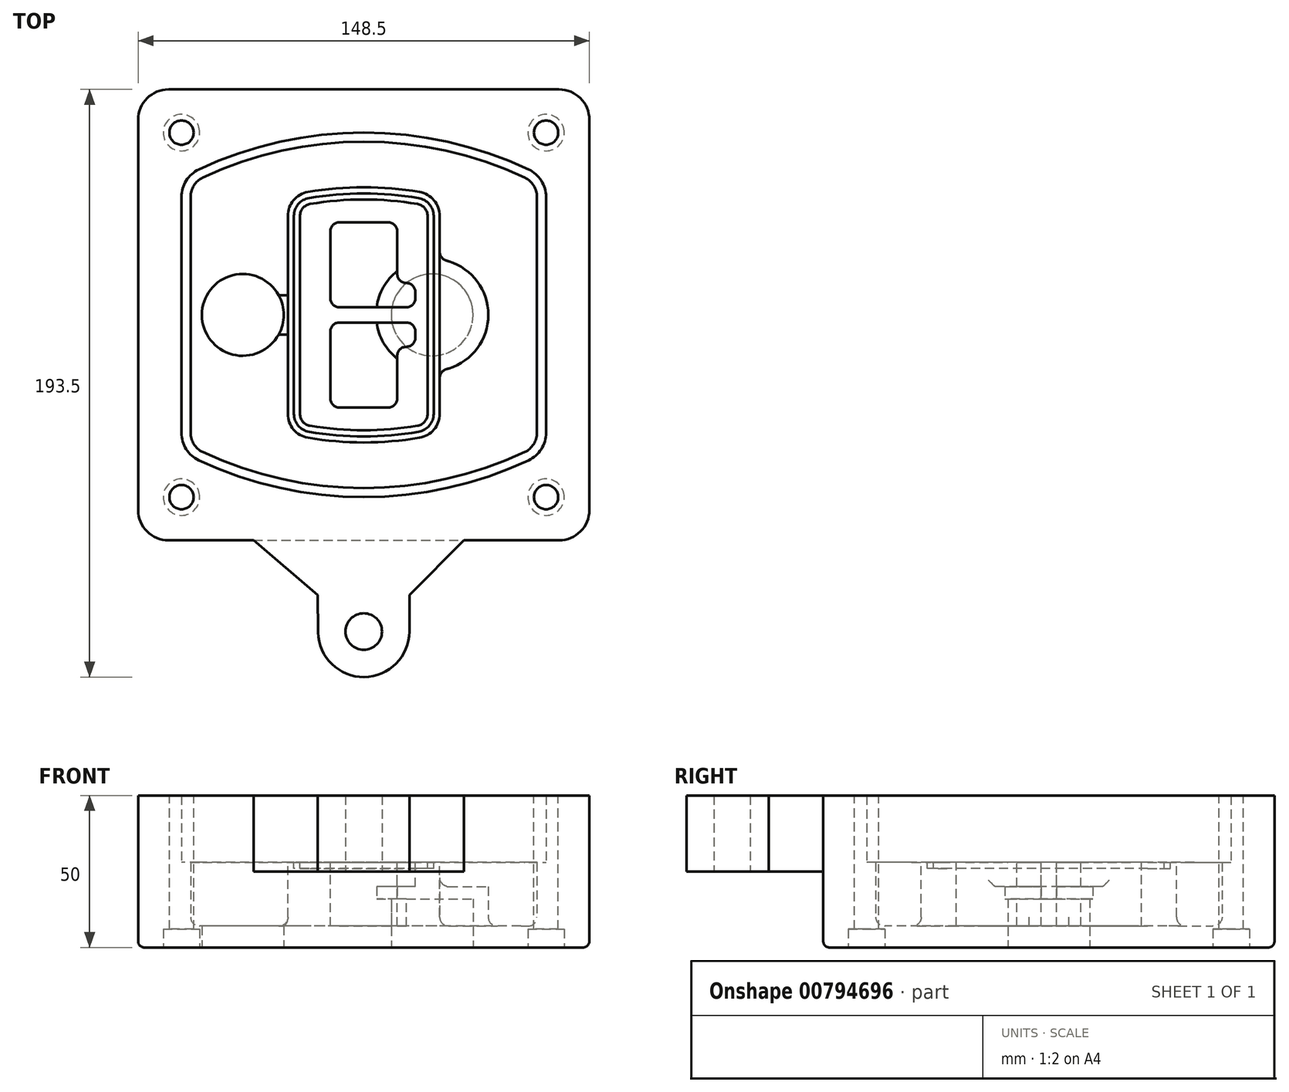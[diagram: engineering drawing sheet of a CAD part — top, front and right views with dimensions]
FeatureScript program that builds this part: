
annotation { "Feature Type Name" : "Feature", "Feature Type Description" : "" }
export const myFeature = defineFeature(function(context is Context, id is Id, definition is map)
    precondition{}
    {
        {
            var Q0;
            Q0=qCreatedBy(makeId("Top.planeOp"),FACE);
            var sketch = newSketch(context, id + "F0", { "sketchPlane" : qUnion([Q0])});
            skPoint(sketch, "E0.rect.middle", {"position": v(0, 0) * mm});
            skLineSegment(sketch, "E1.bottom", {"start": v(-64.25, -74.25) * mm, "end": v(64.25, -74.25) * mm});
            skLineSegment(sketch, "E1.top", {"start": v(-64.25, 74.25) * mm, "end": v(64.25, 74.25) * mm});
            skLineSegment(sketch, "E1.left", {"start": v(-74.25, -64.25) * mm, "end": v(-74.25, 64.25) * mm});
            skLineSegment(sketch, "E1.right", {"start": v(74.25, -64.25) * mm, "end": v(74.25, 64.25) * mm});
            skLineSegment(sketch, "E2", {"start": v(-74.25, 74.25) * mm, "end": v(74.25, -74.25) * mm, "construction": true});
            skLineSegment(sketch, "E3", {"start": v(74.25, 74.25) * mm, "end": v(-74.25, -74.25) * mm, "construction": true});
            skCircle(sketch, "E4", {"center": v(-60, 60) * mm, "radius": 4 * mm});
            skCircle(sketch, "E5", {"center": v(60, 60) * mm, "radius": 4 * mm});
            skCircle(sketch, "E6", {"center": v(60, -60) * mm, "radius": 4 * mm});
            skCircle(sketch, "E7", {"center": v(-60, -60) * mm, "radius": 4 * mm});
            skLineSegment(sketch, "E8", {"start": v(-60, 60) * mm, "end": v(60, 60) * mm, "construction": true});
            skLineSegment(sketch, "E9", {"start": v(60, 60) * mm, "end": v(60, -60) * mm, "construction": true});
            skLineSegment(sketch, "E10", {"start": v(60, -60) * mm, "end": v(-60, -60) * mm, "construction": true});
            skLineSegment(sketch, "E11", {"start": v(-60, -60) * mm, "end": v(-60, 60) * mm, "construction": true});
            skLineSegment(sketch, "E12", {"start": v(-60, 38.83) * mm, "end": v(-60, -38.83) * mm});
            skLineSegment(sketch, "E13", {"start": v(60, 38.83) * mm, "end": v(60, -38.83) * mm});
            skArc(sketch, "E14", {"start": v(54.26, 47.88) * mm, "mid": v(0, 60) * mm, "end": v(-54.26, 47.88) * mm});
            skArc(sketch, "E15", {"start": v(-54.26, -47.88) * mm, "mid": v(0, -60) * mm, "end": v(54.26, -47.88) * mm});
            skLineSegment(sketch, "E16", {"start": v(-60, 0) * mm, "end": v(60, 0) * mm, "construction": true});
            skPoint(sketch, "E17.visualSharp", {"position": v(-60, -45) * mm});
            skArc(sketch, "E17.filletArc", {"start": v(-60, -38.83) * mm, "mid": v(-58.44, -44.2) * mm, "end": v(-54.26, -47.88) * mm});
            skPoint(sketch, "E18.visualSharp", {"position": v(-60, 45) * mm});
            skArc(sketch, "E18.filletArc", {"start": v(-54.26, 47.88) * mm, "mid": v(-58.44, 44.2) * mm, "end": v(-60, 38.83) * mm});
            skPoint(sketch, "E19.visualSharp", {"position": v(60, 45) * mm});
            skArc(sketch, "E19.filletArc", {"start": v(60, 38.83) * mm, "mid": v(58.44, 44.2) * mm, "end": v(54.26, 47.88) * mm});
            skPoint(sketch, "E20.visualSharp", {"position": v(60, -45) * mm});
            skArc(sketch, "E20.filletArc", {"start": v(54.26, -47.88) * mm, "mid": v(58.44, -44.2) * mm, "end": v(60, -38.83) * mm});
            skPoint(sketch, "E21.visualSharp", {"position": v(-74.25, 74.25) * mm});
            skArc(sketch, "E21.filletArc", {"start": v(-64.25, 74.25) * mm, "mid": v(-71.32, 71.32) * mm, "end": v(-74.25, 64.25) * mm});
            skPoint(sketch, "E22.visualSharp", {"position": v(74.25, 74.25) * mm});
            skArc(sketch, "E22.filletArc", {"start": v(74.25, 64.25) * mm, "mid": v(71.32, 71.32) * mm, "end": v(64.25, 74.25) * mm});
            skPoint(sketch, "E23.visualSharp", {"position": v(74.25, -74.25) * mm});
            skArc(sketch, "E23.filletArc", {"start": v(64.25, -74.25) * mm, "mid": v(71.32, -71.32) * mm, "end": v(74.25, -64.25) * mm});
            skPoint(sketch, "E24.visualSharp", {"position": v(-74.25, -74.25) * mm});
            skArc(sketch, "E24.filletArc", {"start": v(-74.25, -64.25) * mm, "mid": v(-71.32, -71.32) * mm, "end": v(-64.25, -74.25) * mm});
            skArc(sketch, "E25.0", {"start": v(57, 38.83) * mm, "mid": v(55.9, 42.58) * mm, "end": v(52.98, 45.17) * mm});
            skLineSegment(sketch, "E25.1", {"start": v(57, 38.83) * mm, "end": v(57, -38.83) * mm});
            skArc(sketch, "E25.2", {"start": v(52.98, -45.17) * mm, "mid": v(55.9, -42.58) * mm, "end": v(57, -38.83) * mm});
            skArc(sketch, "E25.3", {"start": v(-52.98, -45.17) * mm, "mid": v(0, -57) * mm, "end": v(52.98, -45.17) * mm});
            skArc(sketch, "E25.4", {"start": v(-57, -38.83) * mm, "mid": v(-55.9, -42.58) * mm, "end": v(-52.98, -45.17) * mm});
            skArc(sketch, "E25.5", {"start": v(52.98, 45.17) * mm, "mid": v(0, 57) * mm, "end": v(-52.98, 45.17) * mm});
            skLineSegment(sketch, "E25.6", {"start": v(-57, 38.83) * mm, "end": v(-57, -38.83) * mm});
            skArc(sketch, "E25.7", {"start": v(-52.98, 45.17) * mm, "mid": v(-55.9, 42.58) * mm, "end": v(-57, 38.83) * mm});
            skArc(sketch, "E26.0", {"start": v(-55.96, 51.5) * mm, "mid": v(-61.82, 46.33) * mm, "end": v(-64, 38.83) * mm});
            skArc(sketch, "E26.1", {"start": v(55.96, 51.5) * mm, "mid": v(0, 64) * mm, "end": v(-55.96, 51.5) * mm});
            skArc(sketch, "E26.2", {"start": v(64, 38.83) * mm, "mid": v(61.82, 46.33) * mm, "end": v(55.96, 51.5) * mm});
            skLineSegment(sketch, "E26.3", {"start": v(64, 38.83) * mm, "end": v(64, -38.83) * mm});
            skArc(sketch, "E26.4", {"start": v(55.96, -51.5) * mm, "mid": v(61.82, -46.33) * mm, "end": v(64, -38.83) * mm});
            skLineSegment(sketch, "E26.5", {"start": v(-64, 38.83) * mm, "end": v(-64, -38.83) * mm});
            skArc(sketch, "E26.6", {"start": v(-55.96, -51.5) * mm, "mid": v(0, -64) * mm, "end": v(55.96, -51.5) * mm});
            skArc(sketch, "E26.7", {"start": v(-64, -38.83) * mm, "mid": v(-61.82, -46.33) * mm, "end": v(-55.96, -51.5) * mm});
            skSolve(sketch);
        }
        {
            var Q0;
            Q0=makeQuery(id+"F0.imprint","IMPRINT",FACE,{"disambiguationData":[TD([[makeQuery(id+"F0.imprint","IMPRINT",EDGE,{"derivedFrom":sQuery(id+"F0.wireOp",EDGE,"E1.bottom")}),1.0]])]});
            var Q1;
            Q1=makeQuery(id+"F0.imprint","IMPRINT",FACE,{"disambiguationData":[TD([[makeQuery(id+"F0.imprint","IMPRINT",EDGE,{"derivedFrom":sQuery(id+"F0.wireOp",EDGE,"E12")}),1.0]])]});
            var Q2;
            Q2=makeQuery(id+"F0.imprint","IMPRINT",FACE,{"disambiguationData":[TD([[makeQuery(id+"F0.imprint","IMPRINT",EDGE,{"derivedFrom":sQuery(id+"F0.wireOp",EDGE,"E25.0")}),1.0]])]});
            var Q3;
            Q3=makeQuery(id+"F0.imprint","IMPRINT",FACE,{"disambiguationData":[TD([[makeQuery(id+"F0.imprint","IMPRINT",EDGE,{"derivedFrom":sQuery(id+"F0.wireOp",EDGE,"E12")}),-1.0]])]});
            extrude(context, id + "F1", {"entities" : qUnion([Q0, Q1, Q2, Q3]), "oppositeDirection" : true, "depth" : 25 * mm, "offsetDistance" : 25 * mm});
        }
        {
            var Q0;
            Q0=makeQuery(id+"F0.imprint","IMPRINT",FACE,{"disambiguationData":[TD([[makeQuery(id+"F0.imprint","IMPRINT",EDGE,{"derivedFrom":sQuery(id+"F0.wireOp",EDGE,"E12")}),1.0]])]});
            extrude(context, id + "F2", {"entities" : qUnion([Q0]), "operationType" : NewBodyOperationType.ADD, "depth" : 3 * mm});
        }
        {
            var Q0;
            Q0=makeQuery(id+"F0.imprint","IMPRINT",FACE,{"disambiguationData":[TD([[makeQuery(id+"F0.imprint","IMPRINT",EDGE,{"derivedFrom":sQuery(id+"F0.wireOp",EDGE,"E25.0")}),1.0]])]});
            extrude(context, id + "F3", {"entities" : qUnion([Q0]), "operationType" : NewBodyOperationType.REMOVE, "oppositeDirection" : true, "depth" : 18 * mm});
        }
        {
            var Q0;
            Q0=makeQuery(id+"F2.opExtrude","CAP_FACE",FACE,{"disambiguationData":[OSD([sQuery(id+"F0.wireOp",EDGE,"E12"),sQuery(id+"F0.wireOp",EDGE,"E13"),sQuery(id+"F0.wireOp",EDGE,"E14"),sQuery(id+"F0.wireOp",EDGE,"E15"),sQuery(id+"F0.wireOp",EDGE,"E17.filletArc"),sQuery(id+"F0.wireOp",EDGE,"E18.filletArc"),sQuery(id+"F0.wireOp",EDGE,"E19.filletArc"),sQuery(id+"F0.wireOp",EDGE,"E20.filletArc"),sQuery(id+"F0.wireOp",EDGE,"E25.0"),sQuery(id+"F0.wireOp",EDGE,"E25.1"),sQuery(id+"F0.wireOp",EDGE,"E25.2"),sQuery(id+"F0.wireOp",EDGE,"E25.3"),sQuery(id+"F0.wireOp",EDGE,"E25.4"),sQuery(id+"F0.wireOp",EDGE,"E25.5"),sQuery(id+"F0.wireOp",EDGE,"E25.6"),sQuery(id+"F0.wireOp",EDGE,"E25.7")])],"isStart":false});
            var sketch = newSketch(context, id + "F4", { "sketchPlane" : qUnion([Q0])});
            skArc(sketch, "E27.0", {"start": v(-18.34, -40.45) * mm, "mid": v(0, -42) * mm, "end": v(18.34, -40.45) * mm});
            skArc(sketch, "E28.0", {"start": v(18.34, 40.45) * mm, "mid": v(0, 42) * mm, "end": v(-18.34, 40.45) * mm});
            skLineSegment(sketch, "E29", {"start": v(-25, 32.57) * mm, "end": v(-25, -32.57) * mm});
            skLineSegment(sketch, "E30", {"start": v(25, 32.57) * mm, "end": v(25, -32.57) * mm});
            skLineSegment(sketch, "E31", {"start": v(-25, 39.1) * mm, "end": v(25, 39.1) * mm, "construction": true});
            skLineSegment(sketch, "E32", {"start": v(-25, -39.1) * mm, "end": v(25, -39.1) * mm, "construction": true});
            skPoint(sketch, "E33.visualSharp", {"position": v(-25, 39.1) * mm});
            skArc(sketch, "E33.filletArc", {"start": v(-18.34, 40.45) * mm, "mid": v(-23.11, 37.73) * mm, "end": v(-25, 32.57) * mm});
            skPoint(sketch, "E34.visualSharp", {"position": v(25, 39.1) * mm});
            skArc(sketch, "E34.filletArc", {"start": v(25, 32.57) * mm, "mid": v(23.11, 37.73) * mm, "end": v(18.34, 40.45) * mm});
            skPoint(sketch, "E35.visualSharp", {"position": v(25, -39.1) * mm});
            skArc(sketch, "E35.filletArc", {"start": v(18.34, -40.45) * mm, "mid": v(23.11, -37.73) * mm, "end": v(25, -32.57) * mm});
            skPoint(sketch, "E36.visualSharp", {"position": v(-25, -39.1) * mm});
            skArc(sketch, "E36.filletArc", {"start": v(-25, -32.57) * mm, "mid": v(-23.11, -37.73) * mm, "end": v(-18.34, -40.45) * mm});
            skArc(sketch, "E37.0", {"start": v(52.98, 45.17) * mm, "mid": v(0, 57) * mm, "end": v(-52.98, 45.17) * mm});
            skArc(sketch, "E37.1", {"start": v(-52.98, 45.17) * mm, "mid": v(-55.9, 42.58) * mm, "end": v(-57, 38.83) * mm});
            skLineSegment(sketch, "E37.2", {"start": v(-57, 38.83) * mm, "end": v(-57, -38.83) * mm});
            skArc(sketch, "E37.3", {"start": v(-57, -38.83) * mm, "mid": v(-55.9, -42.58) * mm, "end": v(-52.98, -45.17) * mm});
            skArc(sketch, "E37.4", {"start": v(-52.98, -45.17) * mm, "mid": v(0, -57) * mm, "end": v(52.98, -45.17) * mm});
            skArc(sketch, "E37.5", {"start": v(52.98, -45.17) * mm, "mid": v(55.9, -42.58) * mm, "end": v(57, -38.83) * mm});
            skLineSegment(sketch, "E37.6", {"start": v(57, 38.83) * mm, "end": v(57, -38.83) * mm});
            skArc(sketch, "E37.7", {"start": v(57, 38.83) * mm, "mid": v(55.9, 42.58) * mm, "end": v(52.98, 45.17) * mm});
            skLineSegment(sketch, "E38.0", {"start": v(23, 32.57) * mm, "end": v(23, -32.57) * mm});
            skArc(sketch, "E38.1", {"start": v(18, -38.48) * mm, "mid": v(21.58, -36.44) * mm, "end": v(23, -32.57) * mm});
            skArc(sketch, "E38.2", {"start": v(-18, -38.48) * mm, "mid": v(0, -40) * mm, "end": v(18, -38.48) * mm});
            skArc(sketch, "E38.3", {"start": v(-23, -32.57) * mm, "mid": v(-21.58, -36.44) * mm, "end": v(-18, -38.48) * mm});
            skLineSegment(sketch, "E38.4", {"start": v(-23, 32.57) * mm, "end": v(-23, -32.57) * mm});
            skArc(sketch, "E38.5", {"start": v(23, 32.57) * mm, "mid": v(21.58, 36.44) * mm, "end": v(18, 38.48) * mm});
            skArc(sketch, "E38.6", {"start": v(-18, 38.48) * mm, "mid": v(-21.58, 36.44) * mm, "end": v(-23, 32.57) * mm});
            skArc(sketch, "E38.7", {"start": v(18, 38.48) * mm, "mid": v(0, 40) * mm, "end": v(-18, 38.48) * mm});
            skArc(sketch, "E39.0", {"start": v(21, 32.57) * mm, "mid": v(20.06, 35.15) * mm, "end": v(17.67, 36.5) * mm});
            skLineSegment(sketch, "E39.1", {"start": v(21, 32.57) * mm, "end": v(21, -32.57) * mm});
            skArc(sketch, "E39.2", {"start": v(17.67, -36.5) * mm, "mid": v(20.06, -35.15) * mm, "end": v(21, -32.57) * mm});
            skArc(sketch, "E39.3", {"start": v(-17.67, -36.5) * mm, "mid": v(0, -38) * mm, "end": v(17.67, -36.5) * mm});
            skArc(sketch, "E39.4", {"start": v(-21, -32.57) * mm, "mid": v(-20.06, -35.15) * mm, "end": v(-17.67, -36.5) * mm});
            skArc(sketch, "E39.5", {"start": v(17.67, 36.5) * mm, "mid": v(0, 38) * mm, "end": v(-17.67, 36.5) * mm});
            skLineSegment(sketch, "E39.6", {"start": v(-21, 32.57) * mm, "end": v(-21, -32.57) * mm});
            skArc(sketch, "E39.7", {"start": v(-17.67, 36.5) * mm, "mid": v(-20.06, 35.15) * mm, "end": v(-21, 32.57) * mm});
            skLineSegment(sketch, "E40", {"start": v(-25, 0) * mm, "end": v(25, 0) * mm, "construction": true});
            skLineSegment(sketch, "E41", {"start": v(-11, 5.5) * mm, "end": v(-11, 27.5) * mm});
            skLineSegment(sketch, "E42", {"start": v(-8, 30.5) * mm, "end": v(8, 30.5) * mm});
            skLineSegment(sketch, "E43", {"start": v(11, 27.5) * mm, "end": v(11, 13.5) * mm});
            skLineSegment(sketch, "E44", {"start": v(14, 10.5) * mm, "end": v(14, 10.5) * mm});
            skLineSegment(sketch, "E45", {"start": v(17, 7.5) * mm, "end": v(17, 5.5) * mm});
            skLineSegment(sketch, "E46", {"start": v(14, 2.5) * mm, "end": v(-8, 2.5) * mm});
            skPoint(sketch, "E47.visualSharp", {"position": v(-11, 30.5) * mm});
            skArc(sketch, "E47.filletArc", {"start": v(-8, 30.5) * mm, "mid": v(-10.12, 29.62) * mm, "end": v(-11, 27.5) * mm});
            skPoint(sketch, "E48.visualSharp", {"position": v(11, 30.5) * mm});
            skArc(sketch, "E48.filletArc", {"start": v(11, 27.5) * mm, "mid": v(10.12, 29.62) * mm, "end": v(8, 30.5) * mm});
            skPoint(sketch, "E49.visualSharp", {"position": v(11, 10.5) * mm});
            skArc(sketch, "E49.filletArc", {"start": v(11, 13.5) * mm, "mid": v(11.88, 11.38) * mm, "end": v(14, 10.5) * mm});
            skPoint(sketch, "E50.visualSharp", {"position": v(17, 10.5) * mm});
            skArc(sketch, "E50.filletArc", {"start": v(17, 7.5) * mm, "mid": v(16.12, 9.62) * mm, "end": v(14, 10.5) * mm});
            skPoint(sketch, "E51.visualSharp", {"position": v(17, 2.5) * mm});
            skArc(sketch, "E51.filletArc", {"start": v(14, 2.5) * mm, "mid": v(16.12, 3.38) * mm, "end": v(17, 5.5) * mm});
            skPoint(sketch, "E52.visualSharp", {"position": v(-11, 2.5) * mm});
            skArc(sketch, "E52.filletArc", {"start": v(-11, 5.5) * mm, "mid": v(-10.12, 3.38) * mm, "end": v(-8, 2.5) * mm});
            skLineSegment(sketch, "E53.0.MirrorCS", {"start": v(14, -2.5) * mm, "end": v(-8, -2.5) * mm});
            skArc(sketch, "E54.0.MirrorCS", {"start": v(-11, -5.5) * mm, "mid": v(-10.12, -3.38) * mm, "end": v(-8, -2.5) * mm});
            skLineSegment(sketch, "E55.0.MirrorCS", {"start": v(-11, -5.5) * mm, "end": v(-11, -27.5) * mm});
            skArc(sketch, "E56.0.MirrorCS", {"start": v(-8, -30.5) * mm, "mid": v(-10.12, -29.62) * mm, "end": v(-11, -27.5) * mm});
            skLineSegment(sketch, "E57.0.MirrorCS", {"start": v(-8, -30.5) * mm, "end": v(8, -30.5) * mm});
            skArc(sketch, "E58.0.MirrorCS", {"start": v(11, -27.5) * mm, "mid": v(10.12, -29.62) * mm, "end": v(8, -30.5) * mm});
            skLineSegment(sketch, "E59.0.MirrorCS", {"start": v(11, -27.5) * mm, "end": v(11, -13.5) * mm});
            skArc(sketch, "E60.0.MirrorCS", {"start": v(11, -13.5) * mm, "mid": v(11.88, -11.38) * mm, "end": v(14, -10.5) * mm});
            skArc(sketch, "E61.0.MirrorCS", {"start": v(17, -7.5) * mm, "mid": v(16.12, -9.62) * mm, "end": v(14, -10.5) * mm});
            skLineSegment(sketch, "E62.0.MirrorCS", {"start": v(17, -7.5) * mm, "end": v(17, -5.5) * mm});
            skArc(sketch, "E63.0.MirrorCS", {"start": v(14, -2.5) * mm, "mid": v(16.12, -3.38) * mm, "end": v(17, -5.5) * mm});
            skSolve(sketch);
        }
        {
            var Q0;
            Q0=makeQuery(id+"F4.imprint","IMPRINT",FACE,{"disambiguationData":[TD([[makeQuery(id+"F4.imprint","IMPRINT",EDGE,{"derivedFrom":sQuery(id+"F4.wireOp",EDGE,"E27.0")}),1.0]])]});
            var Q1;
            Q1=makeQuery(id+"F4.imprint","IMPRINT",FACE,{"disambiguationData":[TD([[makeQuery(id+"F4.imprint","IMPRINT",EDGE,{"derivedFrom":sQuery(id+"F4.wireOp",EDGE,"E38.0")}),-1.0]])]});
            var Q2;
            Q2=makeQuery(id+"F4.imprint","IMPRINT",FACE,{"disambiguationData":[TD([[makeQuery(id+"F4.imprint","IMPRINT",EDGE,{"derivedFrom":sQuery(id+"F4.wireOp",EDGE,"E39.0")}),1.0]])]});
            extrude(context, id + "F5", {"entities" : qUnion([Q0, Q1, Q2]), "operationType" : NewBodyOperationType.ADD, "endBound" : BoundingType.UP_TO_NEXT, "oppositeDirection" : true, "depth" : 25 * mm});
        }
        {
            var Q0;
            Q0=makeQuery(id+"F4.imprint","IMPRINT",FACE,{"disambiguationData":[TD([[makeQuery(id+"F4.imprint","IMPRINT",EDGE,{"derivedFrom":sQuery(id+"F4.wireOp",EDGE,"E38.0")}),-1.0]])]});
            extrude(context, id + "F6", {"entities" : qUnion([Q0]), "operationType" : NewBodyOperationType.REMOVE, "oppositeDirection" : true, "depth" : 2 * mm});
        }
        {
            var Q0;
            Q0=makeQuery(id+"F1.opExtrude","CAP_FACE",FACE,{"disambiguationData":[OSD([sQuery(id+"F0.wireOp",EDGE,"E1.bottom"),sQuery(id+"F0.wireOp",EDGE,"E1.top"),sQuery(id+"F0.wireOp",EDGE,"E1.left"),sQuery(id+"F0.wireOp",EDGE,"E1.right"),sQuery(id+"F0.wireOp",EDGE,"E4"),sQuery(id+"F0.wireOp",EDGE,"E5"),sQuery(id+"F0.wireOp",EDGE,"E6"),sQuery(id+"F0.wireOp",EDGE,"E7"),sQuery(id+"F0.wireOp",EDGE,"E21.filletArc"),sQuery(id+"F0.wireOp",EDGE,"E22.filletArc"),sQuery(id+"F0.wireOp",EDGE,"E23.filletArc"),sQuery(id+"F0.wireOp",EDGE,"E24.filletArc")])],"isStart":false});
            var sketch = newSketch(context, id + "F7", { "sketchPlane" : qUnion([Q0])});
            skCircle(sketch, "E64", {"center": v(22.5, 0) * mm, "radius": 13.47 * mm});
            skCircle(sketch, "E65", {"center": v(-39.81, 0) * mm, "radius": 13.47 * mm});
            skLineSegment(sketch, "E66", {"start": v(74.25, 0) * mm, "end": v(-74.25, 0) * mm});
            skCircle(sketch, "E67", {"center": v(22.5, 0) * mm, "radius": 18.47 * mm});
            skCircle(sketch, "E68", {"center": v(60, -60) * mm, "radius": 6 * mm});
            skCircle(sketch, "E69", {"center": v(-60, -60) * mm, "radius": 6 * mm});
            skCircle(sketch, "E70", {"center": v(-60, 60) * mm, "radius": 6 * mm});
            skCircle(sketch, "E71", {"center": v(60, 60) * mm, "radius": 6 * mm});
            skSolve(sketch);
        }
        {
            var Q0;
            {var subQ1=sQuery(id+"F7.wireOp",EDGE,"E66");var subQ4=sQuery(id+"F7.wireOp",EDGE,"E64");var subQ6=makeQuery(id+"F7.imprint","INTERSECT",VERTEX,{"disambiguationData":[OD(0.0)],"derivedFrom":[subQ4,subQ1]});Q0=makeQuery(id+"F7.imprint","IMPRINT",FACE,{"disambiguationData":[TD([[makeQuery(id+"F7.imprint","IMPRINT",EDGE,{"disambiguationData":[TD([[subQ6,-1.0]])],"derivedFrom":subQ4}),-1.0]])]});}
            var Q1;
            {var subQ0=sQuery(id+"F7.wireOp",EDGE,"E66");var subQ1=sQuery(id+"F7.wireOp",EDGE,"E64");var subQ3=makeQuery(id+"F7.imprint","INTERSECT",VERTEX,{"disambiguationData":[OD(0.0)],"derivedFrom":[subQ1,subQ0]});Q1=makeQuery(id+"F7.imprint","IMPRINT",FACE,{"disambiguationData":[TD([[makeQuery(id+"F7.imprint","IMPRINT",EDGE,{"disambiguationData":[TD([[subQ3,-1.0]])],"derivedFrom":subQ1}),1.0]])]});}
            var Q2;
            {var subQ0=sQuery(id+"F7.wireOp",EDGE,"E66");var subQ1=sQuery(id+"F7.wireOp",EDGE,"E64");var subQ3=makeQuery(id+"F7.imprint","INTERSECT",VERTEX,{"disambiguationData":[OD(0.0)],"derivedFrom":[subQ1,subQ0]});Q2=makeQuery(id+"F7.imprint","IMPRINT",FACE,{"disambiguationData":[TD([[makeQuery(id+"F7.imprint","IMPRINT",EDGE,{"disambiguationData":[TD([[subQ3,1.0]])],"derivedFrom":subQ1}),1.0]])]});}
            var Q3;
            {var subQ1=sQuery(id+"F7.wireOp",EDGE,"E66");var subQ4=sQuery(id+"F7.wireOp",EDGE,"E64");var subQ6=makeQuery(id+"F7.imprint","INTERSECT",VERTEX,{"disambiguationData":[OD(0.0)],"derivedFrom":[subQ4,subQ1]});Q3=makeQuery(id+"F7.imprint","IMPRINT",FACE,{"disambiguationData":[TD([[makeQuery(id+"F7.imprint","IMPRINT",EDGE,{"disambiguationData":[TD([[subQ6,1.0]])],"derivedFrom":subQ4}),-1.0]])]});}
            extrude(context, id + "F8", {"entities" : qUnion([Q0, Q1, Q2, Q3]), "operationType" : NewBodyOperationType.ADD, "oppositeDirection" : true, "depth" : 20 * mm});
        }
        {
            var Q0;
            {var subQ0=sQuery(id+"F7.wireOp",EDGE,"E66");var subQ1=sQuery(id+"F7.wireOp",EDGE,"E64");var subQ3=makeQuery(id+"F7.imprint","INTERSECT",VERTEX,{"disambiguationData":[OD(0.0)],"derivedFrom":[subQ1,subQ0]});Q0=makeQuery(id+"F7.imprint","IMPRINT",FACE,{"disambiguationData":[TD([[makeQuery(id+"F7.imprint","IMPRINT",EDGE,{"disambiguationData":[TD([[subQ3,-1.0]])],"derivedFrom":subQ1}),1.0]])]});}
            var Q1;
            {var subQ0=sQuery(id+"F7.wireOp",EDGE,"E66");var subQ1=sQuery(id+"F7.wireOp",EDGE,"E64");var subQ3=makeQuery(id+"F7.imprint","INTERSECT",VERTEX,{"disambiguationData":[OD(0.0)],"derivedFrom":[subQ1,subQ0]});Q1=makeQuery(id+"F7.imprint","IMPRINT",FACE,{"disambiguationData":[TD([[makeQuery(id+"F7.imprint","IMPRINT",EDGE,{"disambiguationData":[TD([[subQ3,1.0]])],"derivedFrom":subQ1}),1.0]])]});}
            extrude(context, id + "F9", {"entities" : qUnion([Q0, Q1]), "operationType" : NewBodyOperationType.REMOVE, "oppositeDirection" : true, "depth" : 16 * mm});
        }
        {
            var Q0;
            {var subQ0=sQuery(id+"F7.wireOp",EDGE,"E66");var subQ1=sQuery(id+"F7.wireOp",EDGE,"E65");var subQ3=makeQuery(id+"F7.imprint","INTERSECT",VERTEX,{"disambiguationData":[OD(0.0)],"derivedFrom":[subQ1,subQ0]});Q0=makeQuery(id+"F7.imprint","IMPRINT",FACE,{"disambiguationData":[TD([[makeQuery(id+"F7.imprint","IMPRINT",EDGE,{"disambiguationData":[TD([[subQ3,-1.0]])],"derivedFrom":subQ1}),1.0]])]});}
            var Q1;
            {var subQ0=sQuery(id+"F7.wireOp",EDGE,"E66");var subQ1=sQuery(id+"F7.wireOp",EDGE,"E65");var subQ3=makeQuery(id+"F7.imprint","INTERSECT",VERTEX,{"disambiguationData":[OD(0.0)],"derivedFrom":[subQ1,subQ0]});Q1=makeQuery(id+"F7.imprint","IMPRINT",FACE,{"disambiguationData":[TD([[makeQuery(id+"F7.imprint","IMPRINT",EDGE,{"disambiguationData":[TD([[subQ3,1.0]])],"derivedFrom":subQ1}),1.0]])]});}
            extrude(context, id + "F10", {"entities" : qUnion([Q0, Q1]), "operationType" : NewBodyOperationType.REMOVE, "oppositeDirection" : true, "depth" : 25 * mm});
        }
        {
            var Q0;
            Q0=makeQuery(id+"F7.imprint","IMPRINT",FACE,{"disambiguationData":[TD([[makeQuery(id+"F7.imprint","IMPRINT",EDGE,{"derivedFrom":sQuery(id+"F7.wireOp",EDGE,"E68")}),1.0]])]});
            var Q1;
            Q1=makeQuery(id+"F7.imprint","IMPRINT",FACE,{"disambiguationData":[TD([[makeQuery(id+"F7.imprint","IMPRINT",EDGE,{"derivedFrom":makeQuery(id+"F1.opExtrude","CAP_EDGE",EDGE,{"disambiguationData":[OSD([sQuery(id+"F0.wireOp",EDGE,"E5")])],"isStart":false})}),-1.0]])]});
            var Q2;
            Q2=makeQuery(id+"F7.imprint","IMPRINT",FACE,{"disambiguationData":[TD([[makeQuery(id+"F7.imprint","IMPRINT",EDGE,{"derivedFrom":sQuery(id+"F7.wireOp",EDGE,"E69")}),1.0]])]});
            var Q3;
            Q3=makeQuery(id+"F7.imprint","IMPRINT",FACE,{"disambiguationData":[TD([[makeQuery(id+"F7.imprint","IMPRINT",EDGE,{"derivedFrom":makeQuery(id+"F1.opExtrude","CAP_EDGE",EDGE,{"disambiguationData":[OSD([sQuery(id+"F0.wireOp",EDGE,"E4")])],"isStart":false})}),-1.0]])]});
            var Q4;
            Q4=makeQuery(id+"F7.imprint","IMPRINT",FACE,{"disambiguationData":[TD([[makeQuery(id+"F7.imprint","IMPRINT",EDGE,{"derivedFrom":sQuery(id+"F7.wireOp",EDGE,"E70")}),1.0]])]});
            var Q5;
            Q5=makeQuery(id+"F7.imprint","IMPRINT",FACE,{"disambiguationData":[TD([[makeQuery(id+"F7.imprint","IMPRINT",EDGE,{"derivedFrom":makeQuery(id+"F1.opExtrude","CAP_EDGE",EDGE,{"disambiguationData":[OSD([sQuery(id+"F0.wireOp",EDGE,"E7")])],"isStart":false})}),-1.0]])]});
            var Q6;
            Q6=makeQuery(id+"F7.imprint","IMPRINT",FACE,{"disambiguationData":[TD([[makeQuery(id+"F7.imprint","IMPRINT",EDGE,{"derivedFrom":sQuery(id+"F7.wireOp",EDGE,"E71")}),1.0]])]});
            var Q7;
            Q7=makeQuery(id+"F7.imprint","IMPRINT",FACE,{"disambiguationData":[TD([[makeQuery(id+"F7.imprint","IMPRINT",EDGE,{"derivedFrom":makeQuery(id+"F1.opExtrude","CAP_EDGE",EDGE,{"disambiguationData":[OSD([sQuery(id+"F0.wireOp",EDGE,"E6")])],"isStart":false})}),-1.0]])]});
            extrude(context, id + "F11", {"entities" : qUnion([Q0, Q1, Q2, Q3, Q4, Q5, Q6, Q7]), "operationType" : NewBodyOperationType.REMOVE, "oppositeDirection" : true, "depth" : 6 * mm});
        }
        {
            var Q0;
            Q0=makeQuery(id+"F9.boolean.opBoolean","COPY",FACE,{"derivedFrom":makeQuery(id+"F9.opExtrude","CAP_FACE",FACE,{"disambiguationData":[OSD([sQuery(id+"F7.wireOp",EDGE,"E64")])],"isStart":false})});
            var sketch = newSketch(context, id + "F12", { "sketchPlane" : qUnion([Q0])});
            skArc(sketch, "E72.0", {"start": v(11, 14.45) * mm, "mid": v(6.45, 9.13) * mm, "end": v(4.2, 2.5) * mm});
            skArc(sketch, "E72.1", {"start": v(4.2, -2.5) * mm, "mid": v(6.45, -9.13) * mm, "end": v(11, -14.45) * mm});
            skLineSegment(sketch, "E73", {"start": v(4.2, -2.5) * mm, "end": v(14, -2.5) * mm});
            skLineSegment(sketch, "E74.0", {"start": v(14, 2.5) * mm, "end": v(4.2, 2.5) * mm});
            skArc(sketch, "E74.1", {"start": v(14, 2.5) * mm, "mid": v(16.12, 3.38) * mm, "end": v(17, 5.5) * mm});
            skLineSegment(sketch, "E74.2", {"start": v(17, 7.5) * mm, "end": v(17, 5.5) * mm});
            skArc(sketch, "E74.3", {"start": v(17, 7.5) * mm, "mid": v(16.12, 9.62) * mm, "end": v(14, 10.5) * mm});
            skArc(sketch, "E74.4", {"start": v(11, 13.5) * mm, "mid": v(11.88, 11.38) * mm, "end": v(14, 10.5) * mm});
            skLineSegment(sketch, "E74.5", {"start": v(11, 14.45) * mm, "end": v(11, 13.5) * mm});
            skLineSegment(sketch, "E74.7", {"start": v(14, -2.5) * mm, "end": v(4.2, -2.5) * mm});
            skArc(sketch, "E74.8", {"start": v(14, -2.5) * mm, "mid": v(16.12, -3.38) * mm, "end": v(17, -5.5) * mm});
            skLineSegment(sketch, "E74.9", {"start": v(17, -7.5) * mm, "end": v(17, -5.5) * mm});
            skArc(sketch, "E74.10", {"start": v(17, -7.5) * mm, "mid": v(16.12, -9.62) * mm, "end": v(14, -10.5) * mm});
            skArc(sketch, "E74.11", {"start": v(11, -13.5) * mm, "mid": v(11.88, -11.38) * mm, "end": v(14, -10.5) * mm});
            skLineSegment(sketch, "E74.12", {"start": v(11, -14.45) * mm, "end": v(11, -13.5) * mm});
            skPoint(sketch, "E75.orphan", {"position": v(11, -27.5) * mm});
            skPoint(sketch, "E76.orphan", {"position": v(-8, -2.5) * mm});
            skPoint(sketch, "E77.orphan", {"position": v(-8, 2.5) * mm});
            skPoint(sketch, "E78.orphan", {"position": v(11, 27.5) * mm});
            skSolve(sketch);
        }
        {
            var Q0;
            {var subQ7=sQuery(id+"F12.wireOp",EDGE,"E72.0");var subQ14=sQuery(id+"F12.wireOp",EDGE,"E72.1");var subQ16=sQuery(id+"F12.wireOp",EDGE,"E74.1");var subQ18=sQuery(id+"F12.wireOp",EDGE,"E74.8");Q0=qUnion([makeQuery(id+"F12.imprint","IMPRINT",FACE,{"disambiguationData":[TD([[makeQuery(id+"F12.imprint","IMPRINT",EDGE,{"derivedFrom":subQ7}),1.0]])]}),makeQuery(id+"F12.imprint","IMPRINT",FACE,{"disambiguationData":[TD([[makeQuery(id+"F12.imprint","IMPRINT",EDGE,{"derivedFrom":subQ14}),1.0]])]}),makeQuery(id+"F12.imprint","IMPRINT",FACE,{"disambiguationData":[TD([[makeQuery(id+"F12.imprint","IMPRINT",EDGE,{"derivedFrom":subQ16}),1.0]])]}),makeQuery(id+"F12.imprint","IMPRINT",FACE,{"disambiguationData":[TD([[makeQuery(id+"F12.imprint","IMPRINT",EDGE,{"derivedFrom":subQ18}),-1.0]])]})]);}
            var Q1;
            Q1=makeQuery(id+"F5.boolean.opBoolean","SPLIT",FACE,{"disambiguationData":[TD([makeQuery(id+"F5.opExtrude","SWEPT_FACE",FACE,{"disambiguationData":[OSD([sQuery(id+"F4.wireOp",EDGE,"E41")])]})])],"derivedFrom":makeQuery(id+"F3.boolean.opBoolean","COPY",FACE,{"derivedFrom":makeQuery(id+"F3.opExtrude","CAP_FACE",FACE,{"disambiguationData":[OSD([sQuery(id+"F0.wireOp",EDGE,"E25.0"),sQuery(id+"F0.wireOp",EDGE,"E25.1"),sQuery(id+"F0.wireOp",EDGE,"E25.2"),sQuery(id+"F0.wireOp",EDGE,"E25.3"),sQuery(id+"F0.wireOp",EDGE,"E25.4"),sQuery(id+"F0.wireOp",EDGE,"E25.5"),sQuery(id+"F0.wireOp",EDGE,"E25.6"),sQuery(id+"F0.wireOp",EDGE,"E25.7")])],"isStart":false})})});
            extrude(context, id + "F13", {"entities" : qUnion([Q0]), "operationType" : NewBodyOperationType.REMOVE, "endBound" : BoundingType.UP_TO_SURFACE, "endBoundEntityFace" : qUnion([Q1]), "depth" : 25 * mm});
        }
        {
            var Q0;
            Q0=makeQuery(id+"F3.boolean.opBoolean","COPY",EDGE,{"derivedFrom":makeQuery(id+"F3.opExtrude","CAP_EDGE",EDGE,{"disambiguationData":[OSD([sQuery(id+"F0.wireOp",EDGE,"E25.6")])],"isStart":false})});
            var Q1;
            Q1=makeQuery(id+"F8.boolean.opBoolean","INTERSECT",EDGE,{"derivedFrom":[makeQuery(id+"F5.opExtrude","SWEPT_FACE",FACE,{"disambiguationData":[OSD([sQuery(id+"F4.wireOp",EDGE,"E30")])]}),makeQuery(id+"F8.opExtrude","CAP_FACE",FACE,{"disambiguationData":[OSD([sQuery(id+"F7.wireOp",EDGE,"E67")])],"isStart":false})]});
            var Q2;
            Q2=makeQuery(id+"F8.boolean.opBoolean","INTERSECT",EDGE,{"disambiguationData":[OD(1.0)],"derivedFrom":[makeQuery(id+"F5.opExtrude","SWEPT_FACE",FACE,{"disambiguationData":[OSD([sQuery(id+"F4.wireOp",EDGE,"E30")])]}),makeQuery(id+"F8.opExtrude","SWEPT_FACE",FACE,{"disambiguationData":[OSD([sQuery(id+"F7.wireOp",EDGE,"E67")])]})]});
            var Q3;
            {var subQ0=sQuery(id+"F4.wireOp",EDGE,"E30");Q3=makeQuery(id+"F8.boolean.opBoolean","SPLIT",EDGE,{"disambiguationData":[TD([makeQuery(id+"F5.opExtrude","SWEPT_FACE",FACE,{"disambiguationData":[OSD([sQuery(id+"F4.wireOp",EDGE,"E35.filletArc")])]})])],"derivedFrom":makeQuery(id+"F5.opExtrude","CAP_EDGE",EDGE,{"disambiguationData":[OSD([subQ0])],"isStart":false})});}
            var Q4;
            {var subQ0=sQuery(id+"F0.wireOp",EDGE,"E25.7");var subQ1=sQuery(id+"F0.wireOp",EDGE,"E25.1");var subQ2=sQuery(id+"F0.wireOp",EDGE,"E25.6");var subQ3=sQuery(id+"F0.wireOp",EDGE,"E25.5");var subQ4=sQuery(id+"F0.wireOp",EDGE,"E25.4");var subQ5=sQuery(id+"F0.wireOp",EDGE,"E25.0");var subQ6=sQuery(id+"F0.wireOp",EDGE,"E25.2");var subQ7=sQuery(id+"F0.wireOp",EDGE,"E25.3");Q4=makeQuery(id+"F8.boolean.opBoolean","INTERSECT",EDGE,{"derivedFrom":[makeQuery(id+"F5.boolean.opBoolean","SPLIT",FACE,{"disambiguationData":[TD([makeQuery(id+"F2.opExtrude","SWEPT_FACE",FACE,{"disambiguationData":[OSD([subQ5])]})])],"derivedFrom":makeQuery(id+"F3.boolean.opBoolean","COPY",FACE,{"derivedFrom":makeQuery(id+"F3.opExtrude","CAP_FACE",FACE,{"disambiguationData":[OSD([subQ5,subQ1,subQ6,subQ7,subQ4,subQ3,subQ2,subQ0])],"isStart":false})})}),makeQuery(id+"F8.opExtrude","SWEPT_FACE",FACE,{"disambiguationData":[OSD([sQuery(id+"F7.wireOp",EDGE,"E67")])]})]});}
            var Q5;
            Q5=makeQuery(id+"F8.boolean.opBoolean","INTERSECT",EDGE,{"disambiguationData":[OD(0.0)],"derivedFrom":[makeQuery(id+"F5.opExtrude","SWEPT_FACE",FACE,{"disambiguationData":[OSD([sQuery(id+"F4.wireOp",EDGE,"E30")])]}),makeQuery(id+"F8.opExtrude","SWEPT_FACE",FACE,{"disambiguationData":[OSD([sQuery(id+"F7.wireOp",EDGE,"E67")])]})]});
            fillet(context, id + "F14", {"entities" : qUnion([Q0, Q1, Q2, Q3, Q4, Q5]), "radius" : 3 * mm, "tangentPropagation" : true, "allowEdgeOverflow" : false});
        }
        {
            var Q0;
            Q0=makeQuery(id+"F1.opExtrude","CAP_EDGE",EDGE,{"disambiguationData":[OSD([sQuery(id+"F0.wireOp",EDGE,"E1.bottom")])],"isStart":false});
            fillet(context, id + "F15", {"entities" : qUnion([Q0]), "radius" : 2 * mm, "tangentPropagation" : true, "allowEdgeOverflow" : false});
        }
        {
            var Q0;
            {var subQ0=sQuery(id+"F0.wireOp",EDGE,"E21.filletArc");var subQ1=sQuery(id+"F0.wireOp",EDGE,"E7");var subQ2=sQuery(id+"F0.wireOp",EDGE,"E6");var subQ3=sQuery(id+"F0.wireOp",EDGE,"E5");var subQ4=sQuery(id+"F0.wireOp",EDGE,"E4");var subQ5=sQuery(id+"F0.wireOp",EDGE,"E22.filletArc");var subQ6=sQuery(id+"F0.wireOp",EDGE,"E1.bottom");var subQ7=sQuery(id+"F0.wireOp",EDGE,"E1.right");var subQ8=sQuery(id+"F0.wireOp",EDGE,"E1.top");var subQ9=sQuery(id+"F0.wireOp",EDGE,"E1.left");var subQ10=sQuery(id+"F0.wireOp",EDGE,"E23.filletArc");var subQ11=sQuery(id+"F0.wireOp",EDGE,"E24.filletArc");Q0=makeQuery(id+"F2.boolean.opBoolean","SPLIT",FACE,{"disambiguationData":[TD([makeQuery(id+"F1.opExtrude","SWEPT_FACE",FACE,{"disambiguationData":[OSD([subQ6])]})])],"derivedFrom":makeQuery(id+"F1.opExtrude","CAP_FACE",FACE,{"disambiguationData":[OSD([subQ6,subQ8,subQ9,subQ7,subQ4,subQ3,subQ2,subQ1,subQ0,subQ5,subQ10,subQ11])],"isStart":true})});}
            var sketch = newSketch(context, id + "F16", { "sketchPlane" : qUnion([Q0])});
            skCircle(sketch, "E79", {"center": v(0, -104.25) * mm, "radius": 6 * mm});
            skArc(sketch, "E80", {"start": v(-15, -104.52) * mm, "mid": v(0.14, -119.25) * mm, "end": v(15, -104.25) * mm});
            skLineSegment(sketch, "E81", {"start": v(-15, -104.52) * mm, "end": v(-15.22, -92.25) * mm});
            skLineSegment(sketch, "E82", {"start": v(15, -104.25) * mm, "end": v(15, -92.25) * mm});
            skLineSegment(sketch, "E83", {"start": v(-15.22, -92.25) * mm, "end": v(-36.28, -74.25) * mm});
            skLineSegment(sketch, "E84", {"start": v(15, -92.25) * mm, "end": v(33, -74.25) * mm});
            skLineSegment(sketch, "E85.0", {"start": v(-74.25, -64.25) * mm, "end": v(-74.25, 64.25) * mm});
            skArc(sketch, "E85.1", {"start": v(-64.25, 74.25) * mm, "mid": v(-71.32, 71.32) * mm, "end": v(-74.25, 64.25) * mm});
            skLineSegment(sketch, "E85.2", {"start": v(-64.25, 74.25) * mm, "end": v(64.25, 74.25) * mm});
            skLineSegment(sketch, "E85.3", {"start": v(74.25, -64.25) * mm, "end": v(74.25, 64.25) * mm});
            skArc(sketch, "E85.4", {"start": v(74.25, 64.25) * mm, "mid": v(71.32, 71.32) * mm, "end": v(64.25, 74.25) * mm});
            skArc(sketch, "E85.5", {"start": v(64.25, -74.25) * mm, "mid": v(71.32, -71.32) * mm, "end": v(74.25, -64.25) * mm});
            skLineSegment(sketch, "E85.6", {"start": v(-64.25, -74.25) * mm, "end": v(64.25, -74.25) * mm});
            skArc(sketch, "E85.7", {"start": v(-74.25, -64.25) * mm, "mid": v(-71.32, -71.32) * mm, "end": v(-64.25, -74.25) * mm});
            skCircle(sketch, "E85.8", {"center": v(-60, -60) * mm, "radius": 4 * mm});
            skCircle(sketch, "E85.9", {"center": v(60, -60) * mm, "radius": 4 * mm});
            skCircle(sketch, "E85.10", {"center": v(-60, 60) * mm, "radius": 4 * mm});
            skCircle(sketch, "E85.11", {"center": v(60, 60) * mm, "radius": 4 * mm});
            skPoint(sketch, "E85.12", {"position": v(71.32, 71.32) * mm});
            skLineSegment(sketch, "E86", {"start": v(-74.25, 0) * mm, "end": v(74.25, 0) * mm, "construction": true});
            skArc(sketch, "E87.MirrorCS", {"start": v(-15, 104.52) * mm, "mid": v(0.14, 119.25) * mm, "end": v(15, 104.25) * mm});
            skLineSegment(sketch, "E88.MirrorCS", {"start": v(-15, 104.52) * mm, "end": v(-15.22, 92.25) * mm});
            skArc(sketch, "E89.MirrorCS", {"start": v(64.25, 74.25) * mm, "mid": v(71.32, 71.32) * mm, "end": v(74.25, 64.25) * mm});
            skLineSegment(sketch, "E90.MirrorCS", {"start": v(-15.22, 92.25) * mm, "end": v(-36.28, 74.25) * mm});
            skLineSegment(sketch, "E91.MirrorCS", {"start": v(15, 104.25) * mm, "end": v(15, 92.25) * mm});
            skLineSegment(sketch, "E92.MirrorCS", {"start": v(15, 92.25) * mm, "end": v(33, 74.25) * mm});
            skCircle(sketch, "E93.MirrorC", {"center": v(0, 104.25) * mm, "radius": 6 * mm});
            skArc(sketch, "E94.MirrorCS", {"start": v(-74.25, 64.25) * mm, "mid": v(-71.32, 71.32) * mm, "end": v(-64.25, 74.25) * mm});
            skSolve(sketch);
        }
        {
            var Q0;
            Q0=makeQuery(id+"F16.imprint","IMPRINT",FACE,{"disambiguationData":[TD([[makeQuery(id+"F16.imprint","IMPRINT",EDGE,{"derivedFrom":sQuery(id+"F16.wireOp",EDGE,"E85.0")}),-1.0]])]});
            var Q1;
            Q1=makeQuery(id+"F16.imprint","IMPRINT",FACE,{"disambiguationData":[TD([[makeQuery(id+"F16.imprint","IMPRINT",EDGE,{"derivedFrom":sQuery(id+"F16.wireOp",EDGE,"E79")}),-1.0]])]});
            var Q2;
            Q2=makeQuery(id+"F16.imprint","IMPRINT",FACE,{"disambiguationData":[TD([[makeQuery(id+"F16.imprint","IMPRINT",EDGE,{"derivedFrom":sQuery(id+"F16.wireOp",EDGE,"E87.MirrorCS")}),-1.0]])]});
            extrude(context, id + "F17", {"entities" : qUnion([Q0, Q1, Q2]), "operationType" : NewBodyOperationType.ADD, "depth" : 25 * mm, "offsetDistance" : 25 * mm});
        }
    });
